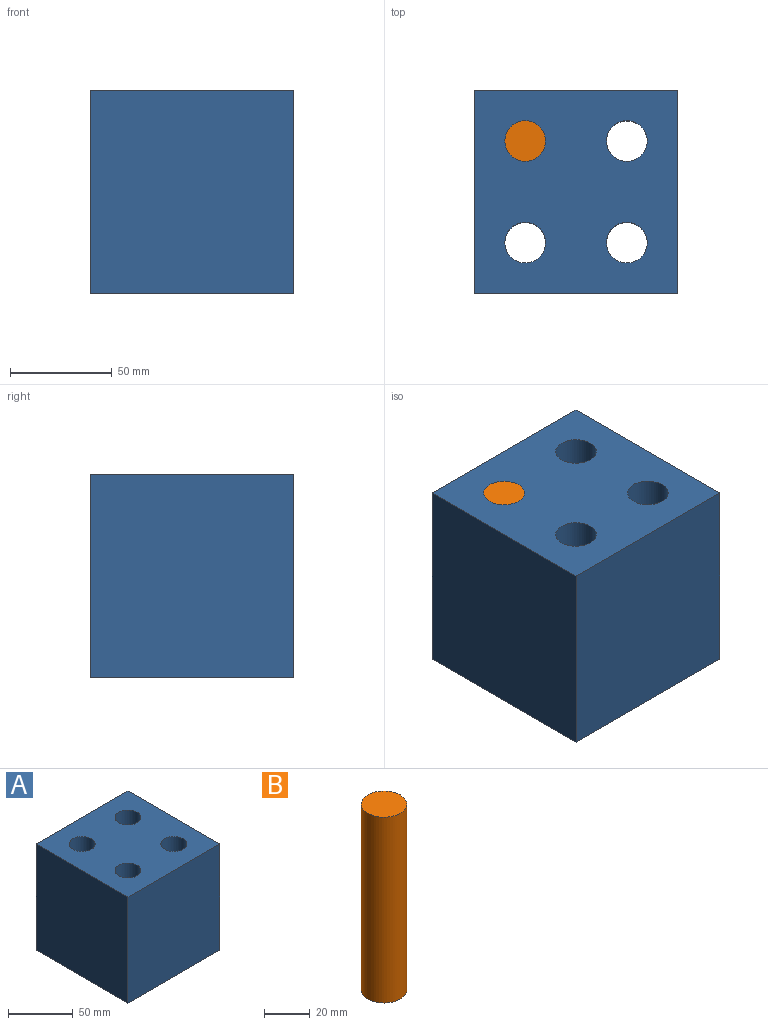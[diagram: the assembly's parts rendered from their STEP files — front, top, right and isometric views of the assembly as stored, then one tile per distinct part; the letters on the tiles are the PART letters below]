
ASSEMBLY  parts=2 mates=1
PART A: 10 faces, bbox 100x100x100 mm
  f0: plane 100x100mm, normal (0,1,0), area 10000mm2, adj f1,f3,f4,f5
  f1: plane 100x100mm, normal (-1,0,0), area 10000mm2, adj f0,f2,f4,f5
  f2: plane 100x100mm, normal (0,-1,0), area 10000mm2, adj f1,f3,f4,f5
  f3: plane 100x100mm, normal (1,0,0), area 10000mm2, adj f0,f2,f4,f5
  f4: plane 100x100mm, normal (0,0,1), area 8743.4mm2, adj f0,f1,f2,f3,f6,f7,f8,f9
  f5: plane 100x100mm, normal (0,0,-1), area 8743.4mm2, adj f0,f1,f2,f3,f6,f7,f8,f9
  f6: cylinder r=10mm len=100mm, axis (0,0,1), area 6283.2mm2, adj f4,f5
  f7: cylinder r=10mm len=100mm, axis (0,0,1), area 6283.2mm2, adj f4,f5
  f8: cylinder r=10mm len=100mm, axis (0,0,1), area 6283.2mm2, adj f4,f5
  f9: cylinder r=10mm len=100mm, axis (0,0,1), area 6283.2mm2, adj f4,f5
PART B: 3 faces, bbox 20x20x100 mm
  f0: cylinder r=10mm len=100mm, axis (0,0,-1), area 6283.2mm2, adj f1,f2
  f1: plane 20x20mm, normal (0,0,1), area 314.2mm2, adj f0
  f2: plane 20x20mm, normal (0,0,-1), area 314.2mm2, adj f0
PLACE A at identity
PLACE B t=(-25,25,0)mm
MATE fastened B.f0 <-> A.f6  axis (0,0,1) through (-25,25,100)mm
